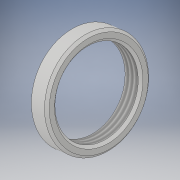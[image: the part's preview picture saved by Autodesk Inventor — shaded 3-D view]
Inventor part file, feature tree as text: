
AUTODESK INVENTOR PART (.ipt)
format: ipt  version: 2018 (Build 220112000, 112)  size: 122,880 bytes
history: native  units: mm
features: extrude x1, chamfer x1, thread x1, sketch x1
ambient origin geometry x8: Origin, YZ Plane, XZ Plane, XY Plane, X Axis, Y Axis, Z Axis, Center Point
bodies: Solid1 (feature_tree)
feature tree (4):
  extrude  "Extrusion1"  Depth=10.0mm
  chamfer  "Chamfer1"  Distance=2.0mm
  thread  "Thread1"  [1 undecoded]
  sketch  "Sketch1"  dims[d0=8.0mm d1=10.0mm d2=2.0mm d3=0.0mm d4=0.25mm d5=2.0mm d6=45.0deg d7=10.0mm d8=0.0mm]
note: 1 required parameter value undecoded (feature->parameter linkage not recoverable at this tier; creation-order binding heuristic only, values carry confidence <= 0.55)
